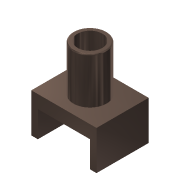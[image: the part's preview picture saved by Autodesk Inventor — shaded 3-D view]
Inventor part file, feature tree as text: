
AUTODESK INVENTOR PART (.ipt)
format: ipt  version: 2015 (Build 190159000, 159)  size: 134,656 bytes
history: native  units: mm
features: extrude x4, sketch x3, hole x1, fillet x1
ambient origin geometry x8: Origin, YZ Plane, XZ Plane, XY Plane, X Axis, Y Axis, Z Axis, Center Point
bodies: Solid1 (feature_tree)
feature tree (9):
  extrude  "Extrusion1"  Depth=40.0mm
  extrude  "Extrusion6"  Depth=10.0mm
  hole  "Hole2"  [1 undecoded]
  fillet  "Fillet3"  Radius=40.0mm
  extrude  "Extrusion8"  Depth=10.0mm TaperAngle=0.0deg
  extrude  "Extrusion9"  Depth=30.0mm TaperAngle=0.0deg
  sketch  "Sketch6"  dims[d6=40.0mm d7=0.0mm d33=25.4mm]
  sketch  "Sketch8"  dims[d34=55.4mm d35=0.0mm d38=10.0mm d39=10.0mm]
  sketch  "Sketch10"  dims[d40=19.0mm d41=6.0mm d42=4.0mm d43=2.0mm d44=90.0deg d45=15.0mm d46=0.0mm d47=1.0mm d49=40.0mm d53=10.0mm d54=0.0mm d61=30.0mm d62=0.0mm]
note: 1 required parameter value undecoded (feature->parameter linkage not recoverable at this tier; creation-order binding heuristic only, values carry confidence <= 0.55)
